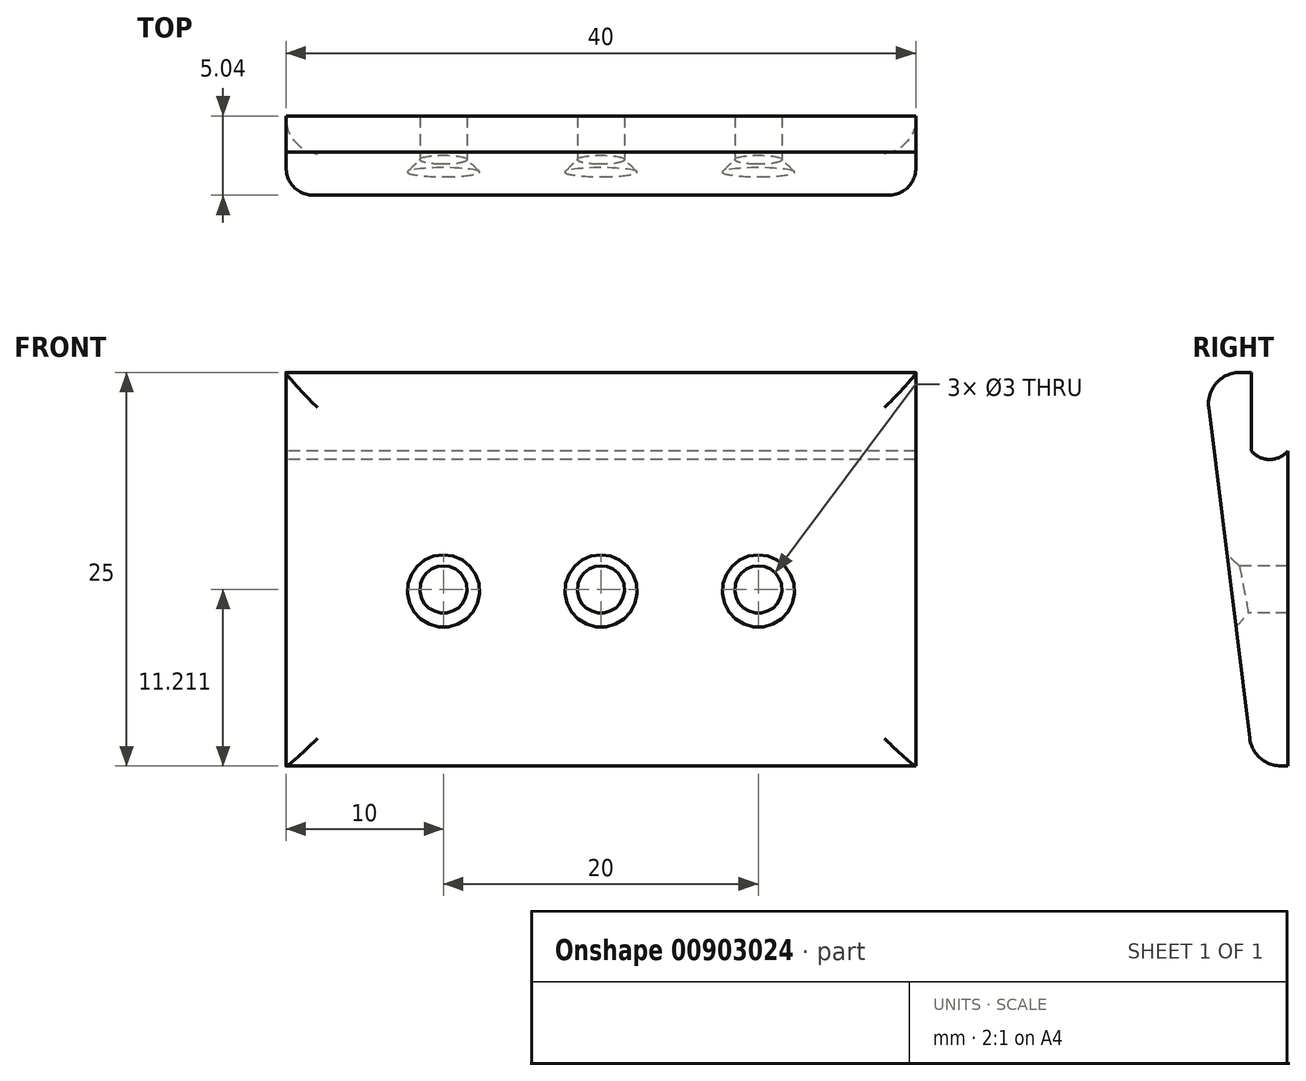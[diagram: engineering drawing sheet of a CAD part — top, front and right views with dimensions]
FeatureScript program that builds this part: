
annotation { "Feature Type Name" : "Feature", "Feature Type Description" : "" }
export const myFeature = defineFeature(function(context is Context, id is Id, definition is map)
    precondition{}
    {
        {
            var Q0;
            Q0=qCreatedBy(makeId("Right.planeOp"),FACE);
            var sketch = newSketch(context, id + "F0", { "sketchPlane" : qUnion([Q0])});
            skLineSegment(sketch, "E0", {"start": v(0, 5) * mm, "end": v(0, 0) * mm});
            skArc(sketch, "E1", {"start": v(0, 0) * mm, "mid": v(1.15, -0.54) * mm, "end": v(2.3, 0) * mm});
            skLineSegment(sketch, "E2", {"start": v(2.3, 0) * mm, "end": v(2.3, -20) * mm});
            skLineSegment(sketch, "E3", {"start": v(2.3, -20) * mm, "end": v(0.1, -20) * mm});
            skLineSegment(sketch, "E4", {"start": v(0.1, -20) * mm, "end": v(-3, 5) * mm});
            skLineSegment(sketch, "E5", {"start": v(-3, 5) * mm, "end": v(0, 5) * mm});
            skSolve(sketch);
        }
        {
            var Q0;
            Q0=makeQuery(id+"F0.imprint","IMPRINT",FACE,{"disambiguationData":[TD([[makeQuery(id+"F0.imprint","IMPRINT",EDGE,{"derivedFrom":sQuery(id+"F0.wireOp",EDGE,"E0")}),-1.0]])]});
            extrude(context, id + "F1", {"entities" : qUnion([Q0]), "depth" : 40 * mm, "offsetDistance" : 25 * mm});
        }
        {
            var Q0;
            Q0=qCreatedBy(makeId("Front.planeOp"),FACE);
            var sketch = newSketch(context, id + "F2", { "sketchPlane" : qUnion([Q0])});
            skCircle(sketch, "E6", {"center": v(10, -8.79) * mm, "radius": 1.5 * mm});
            skCircle(sketch, "E7.1.0.0", {"center": v(20, -8.79) * mm, "radius": 1.5 * mm});
            skCircle(sketch, "E7.2.0.0", {"center": v(30, -8.79) * mm, "radius": 1.5 * mm});
            skLineSegment(sketch, "E7.direction1", {"start": v(10, -8.79) * mm, "end": v(20, -8.79) * mm, "construction": true});
            skLineSegment(sketch, "E8", {"start": v(40, -8.79) * mm, "end": v(30, -8.79) * mm, "construction": true});
            skLineSegment(sketch, "E9", {"start": v(10, -8.79) * mm, "end": v(0, -8.79) * mm, "construction": true});
            skSolve(sketch);
        }
        {
            var Q0;
            Q0=makeQuery(id+"F2.imprint","IMPRINT",FACE,{"disambiguationData":[TD([[makeQuery(id+"F2.imprint","IMPRINT",EDGE,{"derivedFrom":sQuery(id+"F2.wireOp",EDGE,"E7.1.0.0")}),1.0]])]});
            var Q1;
            Q1=makeQuery(id+"F2.imprint","IMPRINT",FACE,{"disambiguationData":[TD([[makeQuery(id+"F2.imprint","IMPRINT",EDGE,{"derivedFrom":sQuery(id+"F2.wireOp",EDGE,"E7.2.0.0")}),1.0]])]});
            var Q2;
            Q2=makeQuery(id+"F2.imprint","IMPRINT",FACE,{"disambiguationData":[TD([[makeQuery(id+"F2.imprint","IMPRINT",EDGE,{"derivedFrom":sQuery(id+"F2.wireOp",EDGE,"E6")}),1.0]])]});
            extrude(context, id + "F3", {"entities" : qUnion([Q0, Q1, Q2]), "operationType" : NewBodyOperationType.REMOVE, "endBound" : BoundingType.SYMMETRIC, "oppositeDirection" : true, "depth" : 25 * mm, "offsetDistance" : 1 * mm});
        }
        {
            var Q0;
            Q0=makeQuery(id+"F1.opExtrude","SWEPT_EDGE",EDGE,{"disambiguationData":[OSD([sQuery(id+"F0.wireOp",EDGE,"E4"),sQuery(id+"F0.wireOp",EDGE,"E5")])]});
            var Q1;
            Q1=makeQuery(id+"F1.opExtrude","SWEPT_EDGE",EDGE,{"disambiguationData":[OSD([sQuery(id+"F0.wireOp",EDGE,"E3"),sQuery(id+"F0.wireOp",EDGE,"E4")])]});
            var Q2;
            Q2=makeQuery(id+"F1.opExtrude","CAP_EDGE",EDGE,{"disambiguationData":[OSD([sQuery(id+"F0.wireOp",EDGE,"E4")])],"isStart":true});
            var Q3;
            Q3=makeQuery(id+"F1.opExtrude","CAP_EDGE",EDGE,{"disambiguationData":[OSD([sQuery(id+"F0.wireOp",EDGE,"E4")])],"isStart":false});
            fillet(context, id + "F4", {"entities" : qUnion([Q0, Q1, Q2, Q3]), "radius" : 2 * mm, "tangentPropagation" : true, "allowEdgeOverflow" : false});
        }
        {
            var Q0;
            Q0=makeQuery(id+"F3.boolean.opBoolean","INTERSECT",EDGE,{"derivedFrom":[makeQuery(id+"F1.opExtrude","SWEPT_FACE",FACE,{"disambiguationData":[OSD([sQuery(id+"F0.wireOp",EDGE,"E4")])]}),makeQuery(id+"F3.opExtrude","SWEPT_FACE",FACE,{"disambiguationData":[OSD([sQuery(id+"F2.wireOp",EDGE,"E6")])]})]});
            var Q1;
            Q1=makeQuery(id+"F3.boolean.opBoolean","INTERSECT",EDGE,{"derivedFrom":[makeQuery(id+"F1.opExtrude","SWEPT_FACE",FACE,{"disambiguationData":[OSD([sQuery(id+"F0.wireOp",EDGE,"E4")])]}),makeQuery(id+"F3.opExtrude","SWEPT_FACE",FACE,{"disambiguationData":[OSD([sQuery(id+"F2.wireOp",EDGE,"E7.1.0.0")])]})]});
            var Q2;
            Q2=makeQuery(id+"F3.boolean.opBoolean","INTERSECT",EDGE,{"derivedFrom":[makeQuery(id+"F1.opExtrude","SWEPT_FACE",FACE,{"disambiguationData":[OSD([sQuery(id+"F0.wireOp",EDGE,"E4")])]}),makeQuery(id+"F3.opExtrude","SWEPT_FACE",FACE,{"disambiguationData":[OSD([sQuery(id+"F2.wireOp",EDGE,"E7.2.0.0")])]})]});
            chamfer(context, id + "F5", {"entities" : qUnion([Q0, Q1, Q2]), "width" : 0.8 * mm, "tangentPropagation" : true});
        }
    });
